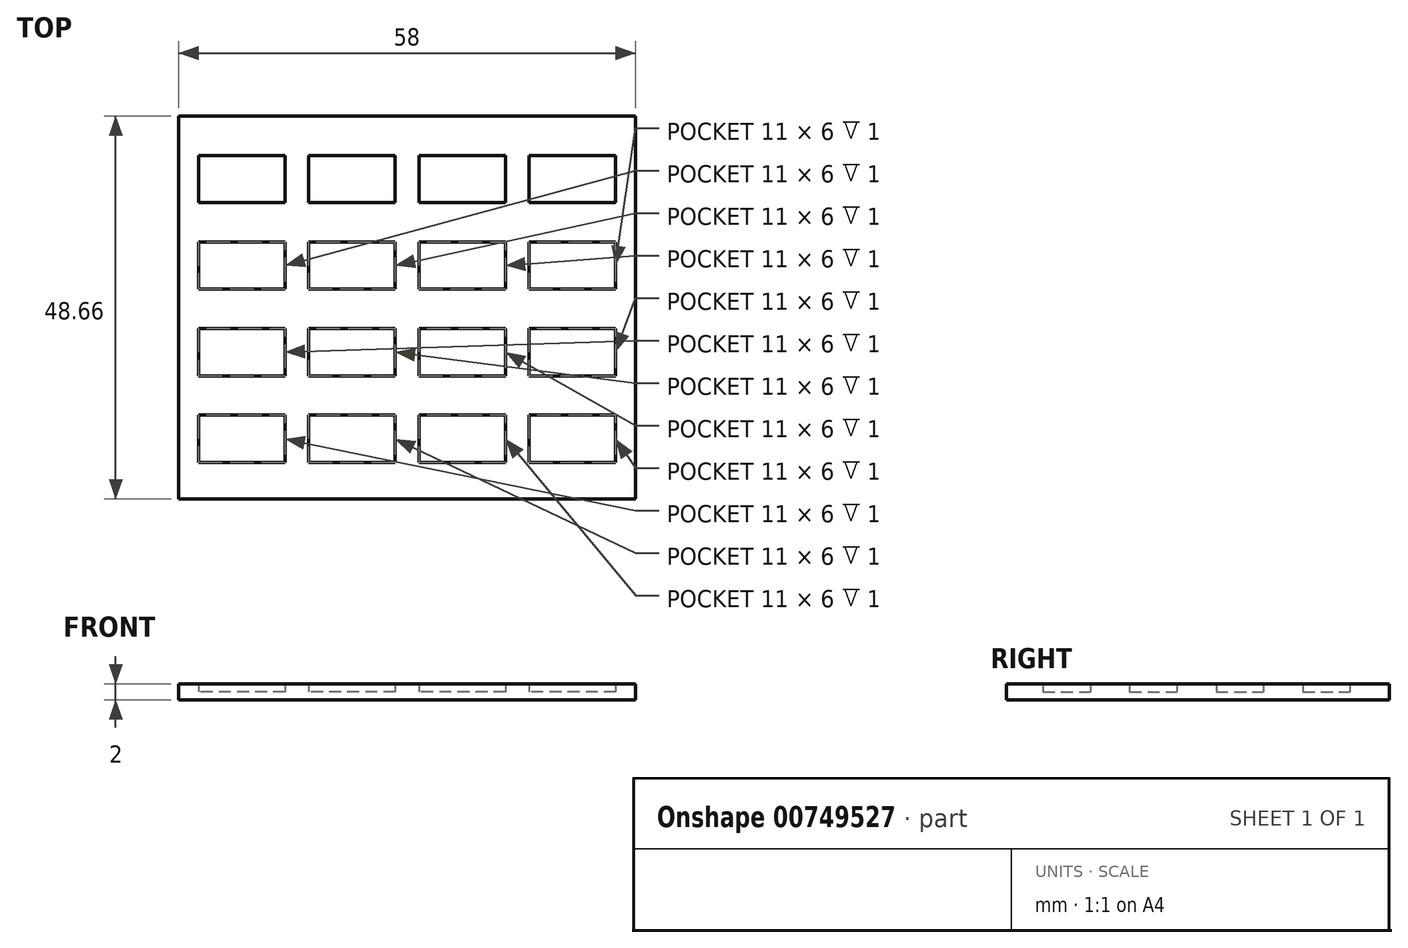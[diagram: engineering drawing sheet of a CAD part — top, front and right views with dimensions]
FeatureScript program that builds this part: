
annotation { "Feature Type Name" : "Feature", "Feature Type Description" : "" }
export const myFeature = defineFeature(function(context is Context, id is Id, definition is map)
    precondition{}
    {
        {
            var Q0;
            Q0=qCreatedBy(makeId("Top.planeOp"),FACE);
            var sketch = newSketch(context, id + "F0", { "sketchPlane" : qUnion([Q0])});
            skLineSegment(sketch, "E0.bottom", {"start": v(29, 24.33) * mm, "end": v(-29, 24.33) * mm});
            skLineSegment(sketch, "E0.top", {"start": v(29, -24.33) * mm, "end": v(-29, -24.33) * mm});
            skLineSegment(sketch, "E0.left", {"start": v(29, 24.33) * mm, "end": v(29, -24.33) * mm});
            skLineSegment(sketch, "E0.right", {"start": v(-29, 24.33) * mm, "end": v(-29, -24.33) * mm});
            skPoint(sketch, "E0.middle", {"position": v(0, 0) * mm});
            skLineSegment(sketch, "E1.bottom", {"start": v(-15.5, 13.33) * mm, "end": v(-26.5, 13.33) * mm});
            skLineSegment(sketch, "E1.top", {"start": v(-15.5, 19.33) * mm, "end": v(-26.5, 19.33) * mm});
            skLineSegment(sketch, "E1.left", {"start": v(-15.5, 13.33) * mm, "end": v(-15.5, 19.33) * mm});
            skLineSegment(sketch, "E1.right", {"start": v(-26.5, 13.33) * mm, "end": v(-26.5, 19.33) * mm});
            skPoint(sketch, "E1.middle", {"position": v(-21, 16.33) * mm});
            skLineSegment(sketch, "E2.1.0.0", {"start": v(-1.5, 13.33) * mm, "end": v(-12.5, 13.33) * mm});
            skLineSegment(sketch, "E2.1.0.1", {"start": v(-1.5, 19.33) * mm, "end": v(-12.5, 19.33) * mm});
            skLineSegment(sketch, "E2.1.0.2", {"start": v(-1.5, 13.33) * mm, "end": v(-1.5, 19.33) * mm});
            skLineSegment(sketch, "E2.1.0.3", {"start": v(-12.5, 13.33) * mm, "end": v(-12.5, 19.33) * mm});
            skPoint(sketch, "E2.1.0.4", {"position": v(-7, 16.33) * mm});
            skLineSegment(sketch, "E2.2.0.0", {"start": v(12.5, 13.33) * mm, "end": v(1.5, 13.33) * mm});
            skLineSegment(sketch, "E2.2.0.1", {"start": v(12.5, 19.33) * mm, "end": v(1.5, 19.33) * mm});
            skLineSegment(sketch, "E2.2.0.2", {"start": v(12.5, 13.33) * mm, "end": v(12.5, 19.33) * mm});
            skLineSegment(sketch, "E2.2.0.3", {"start": v(1.5, 13.33) * mm, "end": v(1.5, 19.33) * mm});
            skPoint(sketch, "E2.2.0.4", {"position": v(7, 16.33) * mm});
            skLineSegment(sketch, "E2.3.0.0", {"start": v(26.5, 13.33) * mm, "end": v(15.5, 13.33) * mm});
            skLineSegment(sketch, "E2.3.0.1", {"start": v(26.5, 19.33) * mm, "end": v(15.5, 19.33) * mm});
            skLineSegment(sketch, "E2.3.0.2", {"start": v(26.5, 13.33) * mm, "end": v(26.5, 19.33) * mm});
            skLineSegment(sketch, "E2.3.0.3", {"start": v(15.5, 13.33) * mm, "end": v(15.5, 19.33) * mm});
            skPoint(sketch, "E2.3.0.4", {"position": v(21, 16.33) * mm});
            skLineSegment(sketch, "E2.direction1", {"start": v(-26.5, 13.33) * mm, "end": v(-12.5, 13.33) * mm, "construction": true});
            skLineSegment(sketch, "E3.1.0.0", {"start": v(-26.5, 2.33) * mm, "end": v(-12.5, 2.33) * mm, "construction": true});
            skLineSegment(sketch, "E3.1.0.1", {"start": v(26.5, 2.33) * mm, "end": v(26.5, 8.33) * mm});
            skLineSegment(sketch, "E3.1.0.2", {"start": v(-26.5, 2.33) * mm, "end": v(-26.5, 8.33) * mm});
            skLineSegment(sketch, "E3.1.0.3", {"start": v(-15.5, 2.33) * mm, "end": v(-15.5, 8.33) * mm});
            skLineSegment(sketch, "E3.1.0.4", {"start": v(-1.5, 2.33) * mm, "end": v(-12.5, 2.33) * mm});
            skLineSegment(sketch, "E3.1.0.5", {"start": v(-1.5, 8.33) * mm, "end": v(-12.5, 8.33) * mm});
            skLineSegment(sketch, "E3.1.0.6", {"start": v(-1.5, 2.33) * mm, "end": v(-1.5, 8.33) * mm});
            skPoint(sketch, "E3.1.0.7", {"position": v(-21, 5.33) * mm});
            skLineSegment(sketch, "E3.1.0.8", {"start": v(12.5, 2.33) * mm, "end": v(1.5, 2.33) * mm});
            skLineSegment(sketch, "E3.1.0.9", {"start": v(-15.5, 8.33) * mm, "end": v(-26.5, 8.33) * mm});
            skLineSegment(sketch, "E3.1.0.10", {"start": v(26.5, 2.33) * mm, "end": v(15.5, 2.33) * mm});
            skPoint(sketch, "E3.1.0.11", {"position": v(7, 5.33) * mm});
            skLineSegment(sketch, "E3.1.0.12", {"start": v(-12.5, 2.33) * mm, "end": v(-12.5, 8.33) * mm});
            skLineSegment(sketch, "E3.1.0.13", {"start": v(1.5, 2.33) * mm, "end": v(1.5, 8.33) * mm});
            skLineSegment(sketch, "E3.1.0.14", {"start": v(12.5, 2.33) * mm, "end": v(12.5, 8.33) * mm});
            skLineSegment(sketch, "E3.1.0.15", {"start": v(12.5, 8.33) * mm, "end": v(1.5, 8.33) * mm});
            skLineSegment(sketch, "E3.1.0.16", {"start": v(26.5, 8.33) * mm, "end": v(15.5, 8.33) * mm});
            skLineSegment(sketch, "E3.1.0.17", {"start": v(15.5, 2.33) * mm, "end": v(15.5, 8.33) * mm});
            skPoint(sketch, "E3.1.0.18", {"position": v(-7, 5.33) * mm});
            skPoint(sketch, "E3.1.0.19", {"position": v(21, 5.33) * mm});
            skLineSegment(sketch, "E3.1.0.20", {"start": v(-15.5, 2.33) * mm, "end": v(-26.5, 2.33) * mm});
            skLineSegment(sketch, "E3.2.0.0", {"start": v(-26.5, -8.67) * mm, "end": v(-12.5, -8.67) * mm, "construction": true});
            skLineSegment(sketch, "E3.2.0.1", {"start": v(26.5, -8.67) * mm, "end": v(26.5, -2.67) * mm});
            skLineSegment(sketch, "E3.2.0.2", {"start": v(-26.5, -8.67) * mm, "end": v(-26.5, -2.67) * mm});
            skLineSegment(sketch, "E3.2.0.3", {"start": v(-15.5, -8.67) * mm, "end": v(-15.5, -2.67) * mm});
            skLineSegment(sketch, "E3.2.0.4", {"start": v(-1.5, -8.67) * mm, "end": v(-12.5, -8.67) * mm});
            skLineSegment(sketch, "E3.2.0.5", {"start": v(-1.5, -2.67) * mm, "end": v(-12.5, -2.67) * mm});
            skLineSegment(sketch, "E3.2.0.6", {"start": v(-1.5, -8.67) * mm, "end": v(-1.5, -2.67) * mm});
            skPoint(sketch, "E3.2.0.7", {"position": v(-21, -5.67) * mm});
            skLineSegment(sketch, "E3.2.0.8", {"start": v(12.5, -8.67) * mm, "end": v(1.5, -8.67) * mm});
            skLineSegment(sketch, "E3.2.0.9", {"start": v(-15.5, -2.67) * mm, "end": v(-26.5, -2.67) * mm});
            skLineSegment(sketch, "E3.2.0.10", {"start": v(26.5, -8.67) * mm, "end": v(15.5, -8.67) * mm});
            skPoint(sketch, "E3.2.0.11", {"position": v(7, -5.67) * mm});
            skLineSegment(sketch, "E3.2.0.12", {"start": v(-12.5, -8.67) * mm, "end": v(-12.5, -2.67) * mm});
            skLineSegment(sketch, "E3.2.0.13", {"start": v(1.5, -8.67) * mm, "end": v(1.5, -2.67) * mm});
            skLineSegment(sketch, "E3.2.0.14", {"start": v(12.5, -8.67) * mm, "end": v(12.5, -2.67) * mm});
            skLineSegment(sketch, "E3.2.0.15", {"start": v(12.5, -2.67) * mm, "end": v(1.5, -2.67) * mm});
            skLineSegment(sketch, "E3.2.0.16", {"start": v(26.5, -2.67) * mm, "end": v(15.5, -2.67) * mm});
            skLineSegment(sketch, "E3.2.0.17", {"start": v(15.5, -8.67) * mm, "end": v(15.5, -2.67) * mm});
            skPoint(sketch, "E3.2.0.18", {"position": v(-7, -5.67) * mm});
            skPoint(sketch, "E3.2.0.19", {"position": v(21, -5.67) * mm});
            skLineSegment(sketch, "E3.2.0.20", {"start": v(-15.5, -8.67) * mm, "end": v(-26.5, -8.67) * mm});
            skLineSegment(sketch, "E3.3.0.0", {"start": v(-26.5, -19.67) * mm, "end": v(-12.5, -19.67) * mm, "construction": true});
            skLineSegment(sketch, "E3.3.0.1", {"start": v(26.5, -19.67) * mm, "end": v(26.5, -13.67) * mm});
            skLineSegment(sketch, "E3.3.0.2", {"start": v(-26.5, -19.67) * mm, "end": v(-26.5, -13.67) * mm});
            skLineSegment(sketch, "E3.3.0.3", {"start": v(-15.5, -19.67) * mm, "end": v(-15.5, -13.67) * mm});
            skLineSegment(sketch, "E3.3.0.4", {"start": v(-1.5, -19.67) * mm, "end": v(-12.5, -19.67) * mm});
            skLineSegment(sketch, "E3.3.0.5", {"start": v(-1.5, -13.67) * mm, "end": v(-12.5, -13.67) * mm});
            skLineSegment(sketch, "E3.3.0.6", {"start": v(-1.5, -19.67) * mm, "end": v(-1.5, -13.67) * mm});
            skPoint(sketch, "E3.3.0.7", {"position": v(-21, -16.67) * mm});
            skLineSegment(sketch, "E3.3.0.8", {"start": v(12.5, -19.67) * mm, "end": v(1.5, -19.67) * mm});
            skLineSegment(sketch, "E3.3.0.9", {"start": v(-15.5, -13.67) * mm, "end": v(-26.5, -13.67) * mm});
            skLineSegment(sketch, "E3.3.0.10", {"start": v(26.5, -19.67) * mm, "end": v(15.5, -19.67) * mm});
            skPoint(sketch, "E3.3.0.11", {"position": v(7, -16.67) * mm});
            skLineSegment(sketch, "E3.3.0.12", {"start": v(-12.5, -19.67) * mm, "end": v(-12.5, -13.67) * mm});
            skLineSegment(sketch, "E3.3.0.13", {"start": v(1.5, -19.67) * mm, "end": v(1.5, -13.67) * mm});
            skLineSegment(sketch, "E3.3.0.14", {"start": v(12.5, -19.67) * mm, "end": v(12.5, -13.67) * mm});
            skLineSegment(sketch, "E3.3.0.15", {"start": v(12.5, -13.67) * mm, "end": v(1.5, -13.67) * mm});
            skLineSegment(sketch, "E3.3.0.16", {"start": v(26.5, -13.67) * mm, "end": v(15.5, -13.67) * mm});
            skLineSegment(sketch, "E3.3.0.17", {"start": v(15.5, -19.67) * mm, "end": v(15.5, -13.67) * mm});
            skPoint(sketch, "E3.3.0.18", {"position": v(-7, -16.67) * mm});
            skPoint(sketch, "E3.3.0.19", {"position": v(21, -16.67) * mm});
            skLineSegment(sketch, "E3.3.0.20", {"start": v(-15.5, -19.67) * mm, "end": v(-26.5, -19.67) * mm});
            skLineSegment(sketch, "E3.direction1", {"start": v(-26.5, 13.33) * mm, "end": v(-26.5, 2.33) * mm, "construction": true});
            skSolve(sketch);
        }
        {
            var Q0;
            Q0=makeQuery(id+"F0.imprint","IMPRINT",FACE,{"disambiguationData":[TD([[makeQuery(id+"F0.imprint","IMPRINT",EDGE,{"derivedFrom":sQuery(id+"F0.wireOp",EDGE,"E0.bottom")}),1.0]])]});
            extrude(context, id + "F1", {"entities" : qUnion([Q0]), "depth" : 2 * mm, "offsetDistance" : 25 * mm});
        }
        {
            var Q0;
            Q0=makeQuery(id+"F0.imprint","IMPRINT",FACE,{"disambiguationData":[TD([[makeQuery(id+"F0.imprint","IMPRINT",EDGE,{"derivedFrom":sQuery(id+"F0.wireOp",EDGE,"E1.bottom")}),-1.0]])]});
            var Q1;
            Q1=makeQuery(id+"F0.imprint","IMPRINT",FACE,{"disambiguationData":[TD([[makeQuery(id+"F0.imprint","IMPRINT",EDGE,{"derivedFrom":sQuery(id+"F0.wireOp",EDGE,"E2.1.0.0")}),-1.0]])]});
            var Q2;
            Q2=makeQuery(id+"F0.imprint","IMPRINT",FACE,{"disambiguationData":[TD([[makeQuery(id+"F0.imprint","IMPRINT",EDGE,{"derivedFrom":sQuery(id+"F0.wireOp",EDGE,"E2.2.0.0")}),-1.0]])]});
            var Q3;
            Q3=makeQuery(id+"F0.imprint","IMPRINT",FACE,{"disambiguationData":[TD([[makeQuery(id+"F0.imprint","IMPRINT",EDGE,{"derivedFrom":sQuery(id+"F0.wireOp",EDGE,"E2.3.0.0")}),-1.0]])]});
            var Q4;
            Q4=makeQuery(id+"F0.imprint","IMPRINT",FACE,{"disambiguationData":[TD([[makeQuery(id+"F0.imprint","IMPRINT",EDGE,{"derivedFrom":sQuery(id+"F0.wireOp",EDGE,"E3.1.0.2")}),-1.0]])]});
            var Q5;
            Q5=makeQuery(id+"F0.imprint","IMPRINT",FACE,{"disambiguationData":[TD([[makeQuery(id+"F0.imprint","IMPRINT",EDGE,{"derivedFrom":sQuery(id+"F0.wireOp",EDGE,"E3.1.0.4")}),-1.0]])]});
            var Q6;
            Q6=makeQuery(id+"F0.imprint","IMPRINT",FACE,{"disambiguationData":[TD([[makeQuery(id+"F0.imprint","IMPRINT",EDGE,{"derivedFrom":sQuery(id+"F0.wireOp",EDGE,"E3.1.0.8")}),-1.0]])]});
            var Q7;
            Q7=makeQuery(id+"F0.imprint","IMPRINT",FACE,{"disambiguationData":[TD([[makeQuery(id+"F0.imprint","IMPRINT",EDGE,{"derivedFrom":sQuery(id+"F0.wireOp",EDGE,"E3.1.0.1")}),1.0]])]});
            var Q8;
            Q8=makeQuery(id+"F0.imprint","IMPRINT",FACE,{"disambiguationData":[TD([[makeQuery(id+"F0.imprint","IMPRINT",EDGE,{"derivedFrom":sQuery(id+"F0.wireOp",EDGE,"E3.2.0.1")}),1.0]])]});
            var Q9;
            Q9=makeQuery(id+"F0.imprint","IMPRINT",FACE,{"disambiguationData":[TD([[makeQuery(id+"F0.imprint","IMPRINT",EDGE,{"derivedFrom":sQuery(id+"F0.wireOp",EDGE,"E3.2.0.8")}),-1.0]])]});
            var Q10;
            Q10=makeQuery(id+"F0.imprint","IMPRINT",FACE,{"disambiguationData":[TD([[makeQuery(id+"F0.imprint","IMPRINT",EDGE,{"derivedFrom":sQuery(id+"F0.wireOp",EDGE,"E3.2.0.4")}),-1.0]])]});
            var Q11;
            Q11=makeQuery(id+"F0.imprint","IMPRINT",FACE,{"disambiguationData":[TD([[makeQuery(id+"F0.imprint","IMPRINT",EDGE,{"derivedFrom":sQuery(id+"F0.wireOp",EDGE,"E3.2.0.2")}),-1.0]])]});
            var Q12;
            Q12=makeQuery(id+"F0.imprint","IMPRINT",FACE,{"disambiguationData":[TD([[makeQuery(id+"F0.imprint","IMPRINT",EDGE,{"derivedFrom":sQuery(id+"F0.wireOp",EDGE,"E3.3.0.2")}),-1.0]])]});
            var Q13;
            Q13=makeQuery(id+"F0.imprint","IMPRINT",FACE,{"disambiguationData":[TD([[makeQuery(id+"F0.imprint","IMPRINT",EDGE,{"derivedFrom":sQuery(id+"F0.wireOp",EDGE,"E3.3.0.4")}),-1.0]])]});
            var Q14;
            Q14=makeQuery(id+"F0.imprint","IMPRINT",FACE,{"disambiguationData":[TD([[makeQuery(id+"F0.imprint","IMPRINT",EDGE,{"derivedFrom":sQuery(id+"F0.wireOp",EDGE,"E3.3.0.8")}),-1.0]])]});
            var Q15;
            Q15=makeQuery(id+"F0.imprint","IMPRINT",FACE,{"disambiguationData":[TD([[makeQuery(id+"F0.imprint","IMPRINT",EDGE,{"derivedFrom":sQuery(id+"F0.wireOp",EDGE,"E3.3.0.1")}),1.0]])]});
            extrude(context, id + "F2", {"entities" : qUnion([Q0, Q1, Q2, Q3, Q4, Q5, Q6, Q7, Q8, Q9, Q10, Q11, Q12, Q13, Q14, Q15]), "operationType" : NewBodyOperationType.ADD, "depth" : 1 * mm, "offsetDistance" : 25 * mm});
        }
    });
